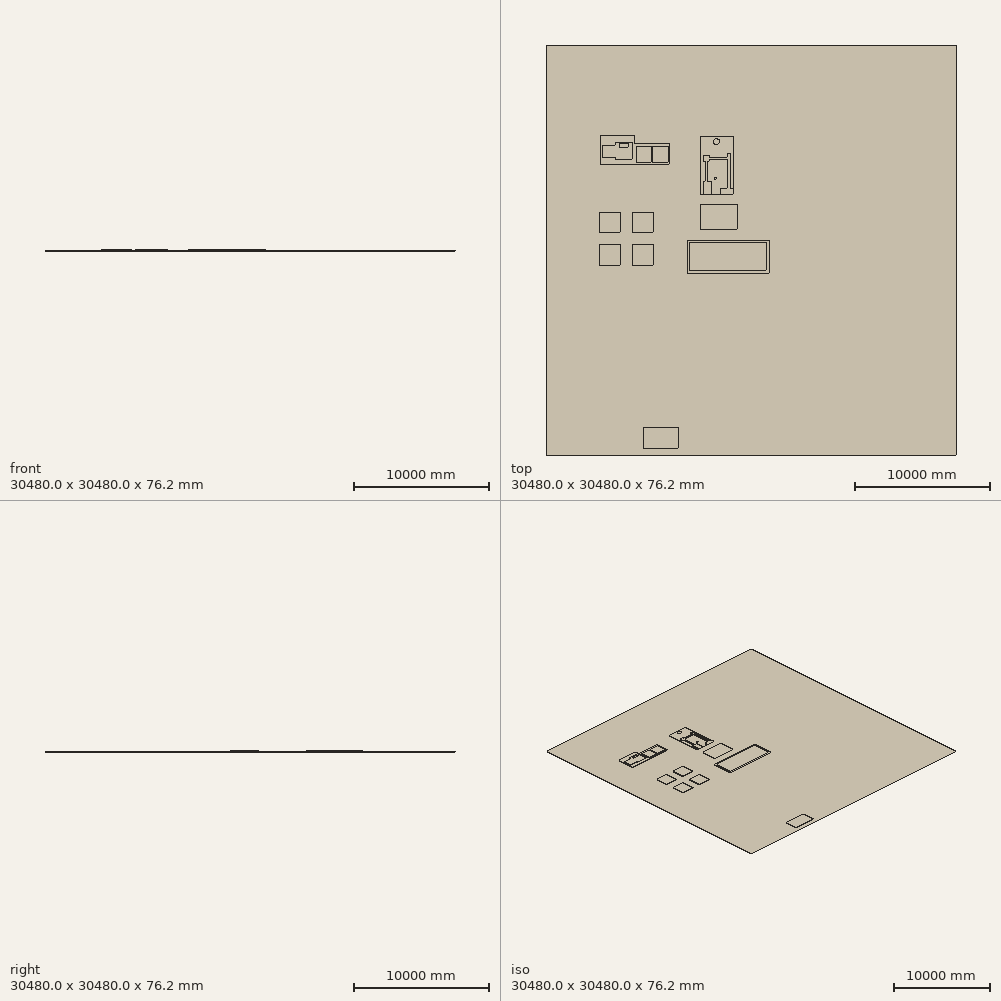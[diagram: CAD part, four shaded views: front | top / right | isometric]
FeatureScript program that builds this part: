
annotation { "Feature Type Name" : "Feature", "Feature Type Description" : "" }
export const myFeature = defineFeature(function(context is Context, id is Id, definition is map)
    precondition{}
    {
        {
            var Q0;
            Q0=qCreatedBy(makeId("Top.planeOp"),FACE);
            var sketch = newSketch(context, id + "F0", { "sketchPlane" : qUnion([Q0])});
            skLineSegment(sketch, "E0.bottom", {"start": v(15240, 15240) * mm, "end": v(-15240, 15240) * mm});
            skLineSegment(sketch, "E0.top", {"start": v(15240, -15240) * mm, "end": v(-15240, -15240) * mm});
            skLineSegment(sketch, "E0.left", {"start": v(15240, 15240) * mm, "end": v(15240, -15240) * mm});
            skLineSegment(sketch, "E0.right", {"start": v(-15240, 15240) * mm, "end": v(-15240, -15240) * mm});
            skPoint(sketch, "E0.middle", {"position": v(0, 0) * mm});
            skSolve(sketch);
        }
        {
            var Q0;
            Q0=qSketchRegion(id+"F0",true);
            extrude(context, id + "F1", {"entities" : qUnion([Q0]), "depth" : 25.4 * mm, "offsetDistance" : 25.4 * mm});
        }
        {
            var Q0;
            Q0=makeQuery(id+"F1.opExtrude","CAP_FACE",FACE,{"disambiguationData":[OSD([sQuery(id+"F0.wireOp",EDGE,"E0.bottom"),sQuery(id+"F0.wireOp",EDGE,"E0.top"),sQuery(id+"F0.wireOp",EDGE,"E0.left"),sQuery(id+"F0.wireOp",EDGE,"E0.right")])],"isStart":false});
            var sketch = newSketch(context, id + "F2", { "sketchPlane" : qUnion([Q0])});
            skLineSegment(sketch, "E1.bottom", {"start": v(-11251.23, 7975.6) * mm, "end": v(-6069.63, 7975.6) * mm});
            skLineSegment(sketch, "E1.top", {"start": v(-11251.23, 6400.8) * mm, "end": v(-6069.63, 6400.8) * mm});
            skLineSegment(sketch, "E1.left", {"start": v(-11251.23, 7975.6) * mm, "end": v(-11251.23, 6400.8) * mm});
            skLineSegment(sketch, "E1.right", {"start": v(-6069.63, 7975.6) * mm, "end": v(-6069.63, 6400.8) * mm});
            skLineSegment(sketch, "E2.bottom", {"start": v(-4789.28, 764.58) * mm, "end": v(1306.72, 764.58) * mm});
            skLineSegment(sketch, "E2.top", {"start": v(-4789.28, -1673.82) * mm, "end": v(1306.72, -1673.82) * mm});
            skLineSegment(sketch, "E2.left", {"start": v(-4789.28, 764.58) * mm, "end": v(-4789.28, -1673.82) * mm});
            skLineSegment(sketch, "E2.right", {"start": v(1306.72, 764.58) * mm, "end": v(1306.72, -1673.82) * mm});
            skLineSegment(sketch, "E3.bottom", {"start": v(-11251.23, 7975.6) * mm, "end": v(-8711.23, 7975.6) * mm});
            skLineSegment(sketch, "E3.top", {"start": v(-11251.23, 8534.4) * mm, "end": v(-8711.23, 8534.4) * mm});
            skLineSegment(sketch, "E3.left", {"start": v(-11251.23, 7975.6) * mm, "end": v(-11251.23, 8534.4) * mm});
            skLineSegment(sketch, "E3.right", {"start": v(-8711.23, 7975.6) * mm, "end": v(-8711.23, 8534.4) * mm});
            skLineSegment(sketch, "E4.bottom", {"start": v(-3812.14, 8461.6) * mm, "end": v(-1373.74, 8461.6) * mm});
            skLineSegment(sketch, "E4.top", {"start": v(-3812.14, 4194.4) * mm, "end": v(-1373.74, 4194.4) * mm});
            skLineSegment(sketch, "E4.left", {"start": v(-3812.14, 8461.6) * mm, "end": v(-3812.14, 4194.4) * mm});
            skLineSegment(sketch, "E4.right", {"start": v(-1373.74, 8461.6) * mm, "end": v(-1373.74, 4194.4) * mm});
            skLineSegment(sketch, "E5.bottom", {"start": v(-8839.2, 2857.06) * mm, "end": v(-7315.2, 2857.06) * mm});
            skLineSegment(sketch, "E5.top", {"start": v(-8839.2, 1333.06) * mm, "end": v(-7315.2, 1333.06) * mm});
            skLineSegment(sketch, "E5.left", {"start": v(-8839.2, 2857.06) * mm, "end": v(-8839.2, 1333.06) * mm});
            skLineSegment(sketch, "E5.right", {"start": v(-7315.2, 2857.06) * mm, "end": v(-7315.2, 1333.06) * mm});
            skLineSegment(sketch, "E6.bottom", {"start": v(-8839.2, 418.66) * mm, "end": v(-7315.2, 418.66) * mm});
            skLineSegment(sketch, "E6.top", {"start": v(-8839.2, -1105.34) * mm, "end": v(-7315.2, -1105.34) * mm});
            skLineSegment(sketch, "E6.left", {"start": v(-8839.2, 418.66) * mm, "end": v(-8839.2, -1105.34) * mm});
            skLineSegment(sketch, "E6.right", {"start": v(-7315.2, 418.66) * mm, "end": v(-7315.2, -1105.34) * mm});
            skLineSegment(sketch, "E7.bottom", {"start": v(-11277.6, 2857.06) * mm, "end": v(-9753.6, 2857.06) * mm});
            skLineSegment(sketch, "E7.top", {"start": v(-11277.6, 1333.06) * mm, "end": v(-9753.6, 1333.06) * mm});
            skLineSegment(sketch, "E7.left", {"start": v(-11277.6, 2857.06) * mm, "end": v(-11277.6, 1333.06) * mm});
            skLineSegment(sketch, "E7.right", {"start": v(-9753.6, 2857.06) * mm, "end": v(-9753.6, 1333.06) * mm});
            skLineSegment(sketch, "E8.bottom", {"start": v(-11277.6, 418.66) * mm, "end": v(-9753.6, 418.66) * mm});
            skLineSegment(sketch, "E8.top", {"start": v(-11277.6, -1105.34) * mm, "end": v(-9753.6, -1105.34) * mm});
            skLineSegment(sketch, "E8.left", {"start": v(-11277.6, 418.66) * mm, "end": v(-11277.6, -1105.34) * mm});
            skLineSegment(sketch, "E8.right", {"start": v(-9753.6, 418.66) * mm, "end": v(-9753.6, -1105.34) * mm});
            skLineSegment(sketch, "E9.bottom", {"start": v(-3811.28, 3421.99) * mm, "end": v(-1068.08, 3421.99) * mm});
            skLineSegment(sketch, "E9.top", {"start": v(-3811.28, 1593.19) * mm, "end": v(-1068.08, 1593.19) * mm});
            skLineSegment(sketch, "E9.left", {"start": v(-3811.28, 3421.99) * mm, "end": v(-3811.28, 1593.19) * mm});
            skLineSegment(sketch, "E9.right", {"start": v(-1068.08, 3421.99) * mm, "end": v(-1068.08, 1593.19) * mm});
            skLineSegment(sketch, "E10.bottom", {"start": v(-8062.16, -13190.43) * mm, "end": v(-5457.19, -13190.43) * mm});
            skLineSegment(sketch, "E10.top", {"start": v(-8062.16, -14725.5) * mm, "end": v(-5457.19, -14725.5) * mm});
            skLineSegment(sketch, "E10.left", {"start": v(-8062.16, -13190.43) * mm, "end": v(-8062.16, -14725.5) * mm});
            skLineSegment(sketch, "E10.right", {"start": v(-5457.19, -13190.43) * mm, "end": v(-5457.19, -14725.5) * mm});
            skSolve(sketch);
        }
        {
            var Q0;
            Q0=qSketchRegion(id+"F2",true);
            extrude(context, id + "F3", {"entities" : qUnion([Q0]), "operationType" : NewBodyOperationType.ADD, "depth" : 25.4 * mm, "offsetDistance" : 25.4 * mm});
        }
        {
            var Q0;
            Q0=makeQuery(id+"F3.opExtrude","CAP_FACE",FACE,{"disambiguationData":[OSD([sQuery(id+"F2.wireOp",EDGE,"E1.bottom"),sQuery(id+"F2.wireOp",EDGE,"E1.top"),sQuery(id+"F2.wireOp",EDGE,"E1.left"),sQuery(id+"F2.wireOp",EDGE,"E1.right"),sQuery(id+"F2.wireOp",EDGE,"biDbiMLD-SDf2-hi3V-axfX-EiKsOqyBmbyk.top"),sQuery(id+"F2.wireOp",EDGE,"biDbiMLD-SDf2-hi3V-axfX-EiKsOqyBmbyk.left"),sQuery(id+"F2.wireOp",EDGE,"biDbiMLD-SDf2-hi3V-axfX-EiKsOqyBmbyk.right")])],"isStart":false});
            var sketch = newSketch(context, id + "F4", { "sketchPlane" : qUnion([Q0])});
            skPoint(sketch, "E11.centerSnap0", {"position": v(-6069.63, 7188.2) * mm});
            skLineSegment(sketch, "E12.bottom", {"start": v(-2338.94, 4575.4) * mm, "end": v(-1373.74, 4575.4) * mm});
            skLineSegment(sketch, "E12.top", {"start": v(-2338.94, 4194.4) * mm, "end": v(-1373.74, 4194.4) * mm});
            skLineSegment(sketch, "E12.left", {"start": v(-2338.94, 4575.4) * mm, "end": v(-2338.94, 4194.4) * mm});
            skLineSegment(sketch, "E12.right", {"start": v(-1373.74, 4575.4) * mm, "end": v(-1373.74, 4194.4) * mm});
            skLineSegment(sketch, "E13.bottom", {"start": v(-11048.03, 7594.6) * mm, "end": v(-10133.63, 7594.6) * mm});
            skLineSegment(sketch, "E13.top", {"start": v(-11048.03, 7086.6) * mm, "end": v(-10133.63, 7086.6) * mm});
            skLineSegment(sketch, "E13.left", {"start": v(-11048.03, 7594.6) * mm, "end": v(-11048.03, 7086.6) * mm});
            skLineSegment(sketch, "E13.right", {"start": v(-10133.63, 7594.6) * mm, "end": v(-10133.63, 7086.6) * mm});
            skLineSegment(sketch, "E14.bottom", {"start": v(-10133.63, 8051.8) * mm, "end": v(-8863.63, 8051.8) * mm});
            skLineSegment(sketch, "E14.top", {"start": v(-10133.63, 6781.8) * mm, "end": v(-8863.63, 6781.8) * mm});
            skLineSegment(sketch, "E14.left", {"start": v(-10133.63, 8051.8) * mm, "end": v(-10133.63, 6781.8) * mm});
            skLineSegment(sketch, "E14.right", {"start": v(-8863.63, 8051.8) * mm, "end": v(-8863.63, 6781.8) * mm});
            skLineSegment(sketch, "E15.bottom", {"start": v(-9803.43, 7924.8) * mm, "end": v(-9168.43, 7924.8) * mm});
            skLineSegment(sketch, "E15.top", {"start": v(-9803.43, 7620) * mm, "end": v(-9168.43, 7620) * mm});
            skLineSegment(sketch, "E15.left", {"start": v(-9803.43, 7924.8) * mm, "end": v(-9803.43, 7620) * mm});
            skLineSegment(sketch, "E15.right", {"start": v(-9168.43, 7924.8) * mm, "end": v(-9168.43, 7620) * mm});
            skLineSegment(sketch, "E16.bottom", {"start": v(-11048.03, 7797.8) * mm, "end": v(-10133.63, 7797.8) * mm});
            skLineSegment(sketch, "E16.top", {"start": v(-11048.03, 6883.4) * mm, "end": v(-10133.63, 6883.4) * mm});
            skLineSegment(sketch, "E16.left", {"start": v(-11048.03, 7797.8) * mm, "end": v(-11048.03, 6883.4) * mm});
            skLineSegment(sketch, "E16.right", {"start": v(-10133.63, 7797.8) * mm, "end": v(-10133.63, 6883.4) * mm});
            skLineSegment(sketch, "E17.bottom", {"start": v(-8584.23, 7721.6) * mm, "end": v(-7441.23, 7721.6) * mm});
            skLineSegment(sketch, "E17.top", {"start": v(-8584.23, 6578.6) * mm, "end": v(-7441.23, 6578.6) * mm});
            skLineSegment(sketch, "E17.left", {"start": v(-8584.23, 7721.6) * mm, "end": v(-8584.23, 6578.6) * mm});
            skLineSegment(sketch, "E17.right", {"start": v(-7441.23, 7721.6) * mm, "end": v(-7441.23, 6578.6) * mm});
            skLineSegment(sketch, "E18.bottom", {"start": v(-7339.63, 7721.6) * mm, "end": v(-6196.63, 7721.6) * mm});
            skLineSegment(sketch, "E18.top", {"start": v(-7339.63, 6578.6) * mm, "end": v(-6196.63, 6578.6) * mm});
            skLineSegment(sketch, "E18.left", {"start": v(-7339.63, 7721.6) * mm, "end": v(-7339.63, 6578.6) * mm});
            skLineSegment(sketch, "E18.right", {"start": v(-6196.63, 7721.6) * mm, "end": v(-6196.63, 6578.6) * mm});
            skLineSegment(sketch, "E19.bottom", {"start": v(-3598.78, 4194.4) * mm, "end": v(-2989.18, 4194.4) * mm});
            skLineSegment(sketch, "E19.top", {"start": v(-3598.78, 5108.8) * mm, "end": v(-2989.18, 5108.8) * mm});
            skLineSegment(sketch, "E19.left", {"start": v(-3598.78, 4194.4) * mm, "end": v(-3598.78, 5108.8) * mm});
            skLineSegment(sketch, "E19.right", {"start": v(-2989.18, 4194.4) * mm, "end": v(-2989.18, 5108.8) * mm});
            skPoint(sketch, "E20.oppositeSnap0", {"position": v(-3293.98, 5108.8) * mm});
            skLineSegment(sketch, "E20.bottom", {"start": v(-3415.9, 5108.8) * mm, "end": v(-3293.98, 5108.8) * mm});
            skLineSegment(sketch, "E20.top", {"start": v(-3415.9, 6632.8) * mm, "end": v(-3293.98, 6632.8) * mm});
            skLineSegment(sketch, "E20.left", {"start": v(-3415.9, 5108.8) * mm, "end": v(-3415.9, 6632.8) * mm});
            skLineSegment(sketch, "E20.right", {"start": v(-3293.98, 5108.8) * mm, "end": v(-3293.98, 6632.8) * mm});
            skLineSegment(sketch, "E21.bottom", {"start": v(-3598.78, 6632.8) * mm, "end": v(-3141.58, 6632.8) * mm});
            skLineSegment(sketch, "E21.top", {"start": v(-3598.78, 7090) * mm, "end": v(-3141.58, 7090) * mm});
            skLineSegment(sketch, "E21.left", {"start": v(-3598.78, 6632.8) * mm, "end": v(-3598.78, 7090) * mm});
            skLineSegment(sketch, "E21.right", {"start": v(-3141.58, 6632.8) * mm, "end": v(-3141.58, 7090) * mm});
            skLineSegment(sketch, "E22.bottom", {"start": v(-1800.46, 7242.4) * mm, "end": v(-1587.1, 7242.4) * mm});
            skLineSegment(sketch, "E22.top", {"start": v(-1800.46, 4194.4) * mm, "end": v(-1587.1, 4194.4) * mm});
            skLineSegment(sketch, "E22.left", {"start": v(-1800.46, 7242.4) * mm, "end": v(-1800.46, 4194.4) * mm});
            skLineSegment(sketch, "E22.right", {"start": v(-1587.1, 7242.4) * mm, "end": v(-1587.1, 4194.4) * mm});
            skCircle(sketch, "E23", {"center": v(-2592.94, 8080.6) * mm, "radius": 228.6 * mm});
            skLineSegment(sketch, "E24.bottom", {"start": v(-3141.58, 6937.6) * mm, "end": v(-1800.46, 6937.6) * mm});
            skLineSegment(sketch, "E24.top", {"start": v(-3141.58, 6754.72) * mm, "end": v(-1800.46, 6754.72) * mm});
            skLineSegment(sketch, "E24.left", {"start": v(-3141.58, 6937.6) * mm, "end": v(-3141.58, 6754.72) * mm});
            skLineSegment(sketch, "E24.right", {"start": v(-1800.46, 6937.6) * mm, "end": v(-1800.46, 6754.72) * mm});
            skLineSegment(sketch, "E25.bottom", {"start": v(-2760.58, 5413.6) * mm, "end": v(-2608.18, 5413.6) * mm});
            skLineSegment(sketch, "E25.top", {"start": v(-2760.58, 5261.2) * mm, "end": v(-2608.18, 5261.2) * mm});
            skLineSegment(sketch, "E25.left", {"start": v(-2760.58, 5413.6) * mm, "end": v(-2760.58, 5261.2) * mm});
            skLineSegment(sketch, "E25.right", {"start": v(-2608.18, 5413.6) * mm, "end": v(-2608.18, 5261.2) * mm});
            skLineSegment(sketch, "E26.bottom", {"start": v(-4585.06, 560.36) * mm, "end": v(1102.5, 560.36) * mm});
            skLineSegment(sketch, "E26.top", {"start": v(-4585.06, -1469.6) * mm, "end": v(1102.5, -1469.6) * mm});
            skLineSegment(sketch, "E26.left", {"start": v(-4585.06, 560.36) * mm, "end": v(-4585.06, -1469.6) * mm});
            skLineSegment(sketch, "E26.right", {"start": v(1102.5, 560.36) * mm, "end": v(1102.5, -1469.6) * mm});
            skSolve(sketch);
        }
        {
            var Q0;
            Q0=qSketchRegion(id+"F4",true);
            extrude(context, id + "F5", {"entities" : qUnion([Q0]), "operationType" : NewBodyOperationType.ADD, "depth" : 25.4 * mm, "offsetDistance" : 25.4 * mm});
        }
    });
